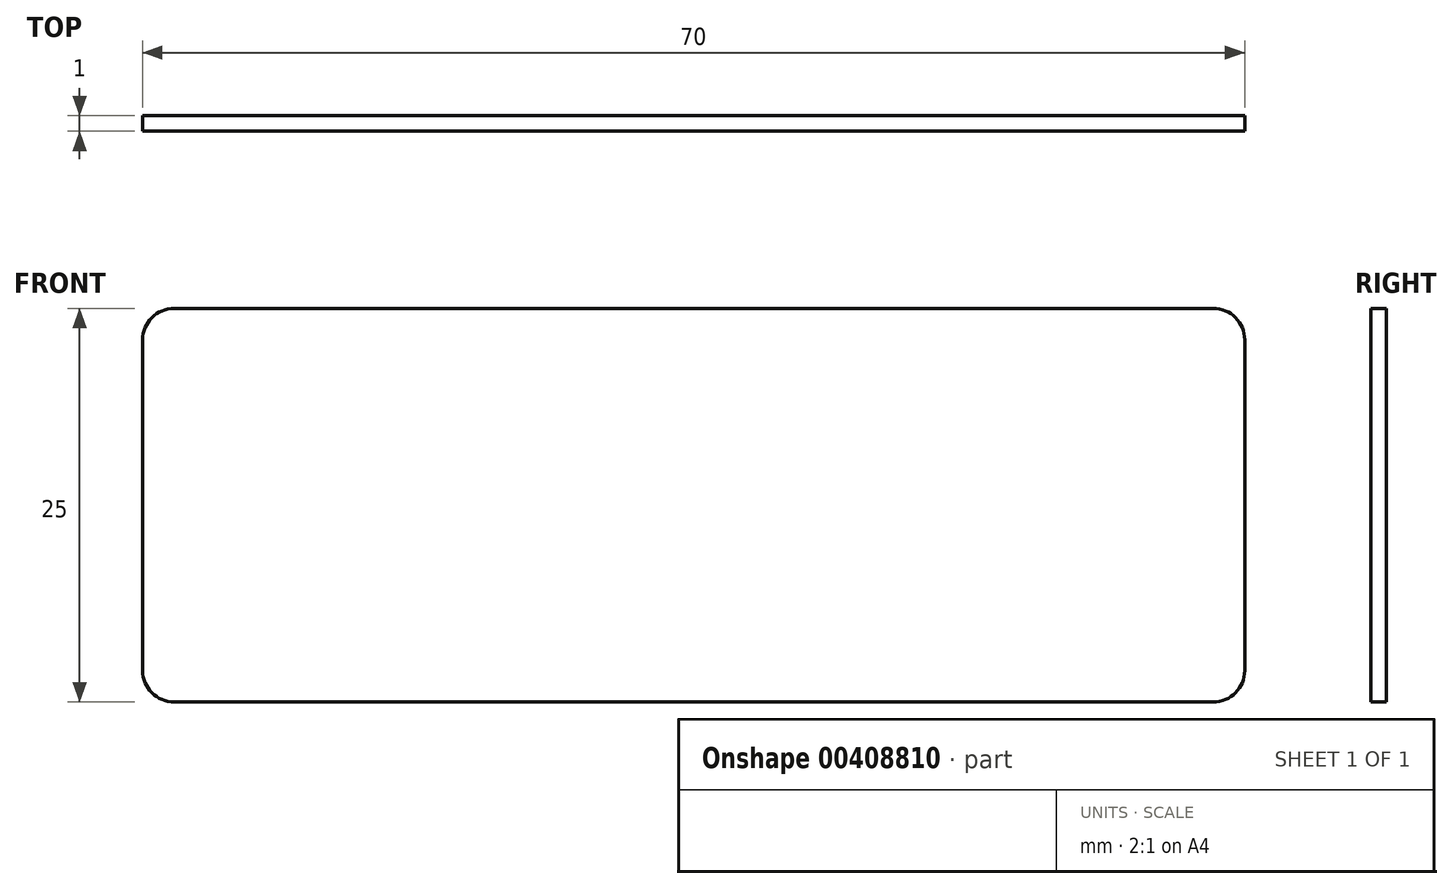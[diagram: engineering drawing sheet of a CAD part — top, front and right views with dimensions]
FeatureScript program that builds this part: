
annotation { "Feature Type Name" : "Feature", "Feature Type Description" : "" }
export const myFeature = defineFeature(function(context is Context, id is Id, definition is map)
    precondition{}
    {
        {
            var Q0;
            Q0=qCreatedBy(makeId("Front.planeOp"),FACE);
            var sketch = newSketch(context, id + "F0", { "sketchPlane" : qUnion([Q0])});
            skLineSegment(sketch, "E0.bottom", {"start": v(35, -12.5) * mm, "end": v(-35, -12.5) * mm});
            skLineSegment(sketch, "E0.top", {"start": v(35, 12.5) * mm, "end": v(-35, 12.5) * mm});
            skLineSegment(sketch, "E0.left", {"start": v(35, -12.5) * mm, "end": v(35, 12.5) * mm});
            skLineSegment(sketch, "E0.right", {"start": v(-35, -12.5) * mm, "end": v(-35, 12.5) * mm});
            skPoint(sketch, "E0.middle", {"position": v(0, 0) * mm});
            skSolve(sketch);
        }
        {
            var Q0;
            Q0=makeQuery(id+"F0.imprint","IMPRINT",FACE,{"disambiguationData":[TD([[makeQuery(id+"F0.imprint","IMPRINT",EDGE,{"derivedFrom":sQuery(id+"F0.wireOp",EDGE,"E0.bottom")}),-1.0]])]});
            extrude(context, id + "F1", {"entities" : qUnion([Q0]), "depth" : 1 * mm, "symmetric" : true});
        }
        {
            var Q0;
            Q0=makeQuery(id+"F1.opExtrude","SWEPT_EDGE",EDGE,{"disambiguationData":[OSD([sQuery(id+"F0.wireOp",EDGE,"E0.bottom"),sQuery(id+"F0.wireOp",EDGE,"E0.right")])]});
            var Q1;
            Q1=makeQuery(id+"F1.opExtrude","SWEPT_EDGE",EDGE,{"disambiguationData":[OSD([sQuery(id+"F0.wireOp",EDGE,"E0.top"),sQuery(id+"F0.wireOp",EDGE,"E0.right")])]});
            var Q2;
            Q2=makeQuery(id+"F1.opExtrude","SWEPT_EDGE",EDGE,{"disambiguationData":[OSD([sQuery(id+"F0.wireOp",EDGE,"E0.top"),sQuery(id+"F0.wireOp",EDGE,"E0.left")])]});
            var Q3;
            Q3=makeQuery(id+"F1.opExtrude","SWEPT_EDGE",EDGE,{"disambiguationData":[OSD([sQuery(id+"F0.wireOp",EDGE,"E0.bottom"),sQuery(id+"F0.wireOp",EDGE,"E0.left")])]});
            fillet(context, id + "F2", {"entities" : qUnion([Q0, Q1, Q2, Q3]), "radius" : 2 * mm, "tangentPropagation" : true, "allowEdgeOverflow" : false});
        }
    });
